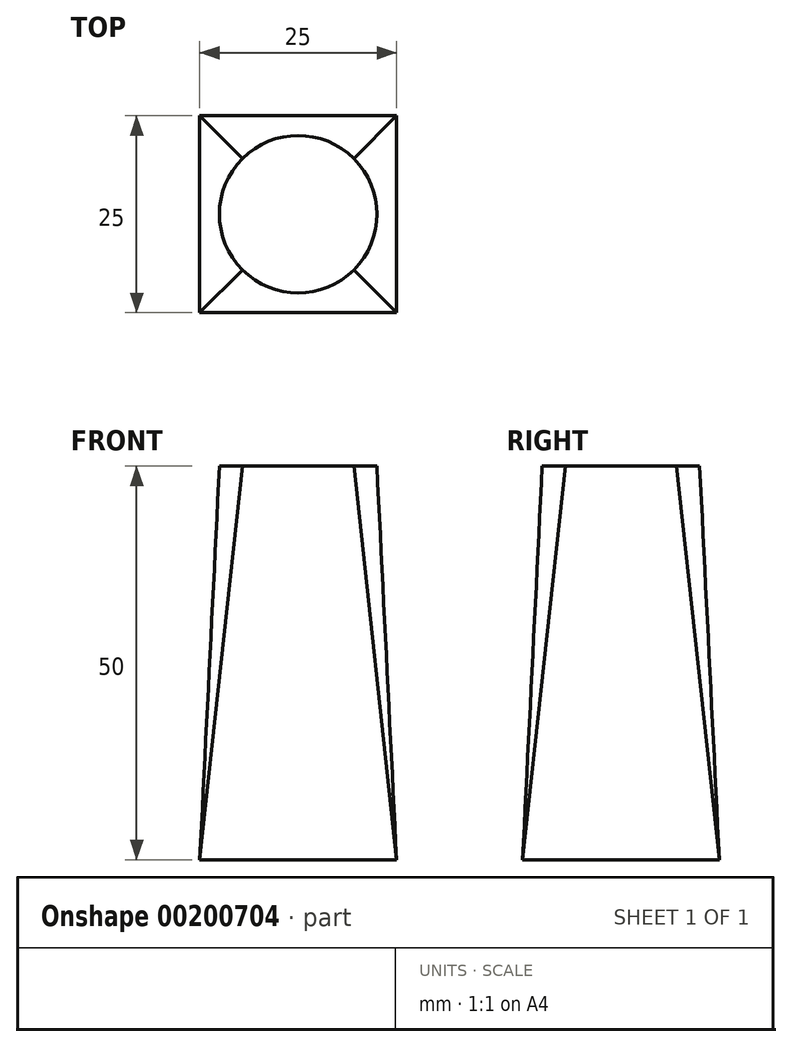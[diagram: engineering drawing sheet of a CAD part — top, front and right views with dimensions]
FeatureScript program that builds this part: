
annotation { "Feature Type Name" : "Feature", "Feature Type Description" : "" }
export const myFeature = defineFeature(function(context is Context, id is Id, definition is map)
    precondition{}
    {
        {
            var Q0;
            Q0=qCreatedBy(makeId("Top.planeOp"),FACE);
            var sketch = newSketch(context, id + "F0", { "sketchPlane" : qUnion([Q0])});
            skLineSegment(sketch, "E0.bottom", {"start": v(-24.37, -23.4) * mm, "end": v(0.63, -23.4) * mm});
            skLineSegment(sketch, "E0.top", {"start": v(-24.37, 1.6) * mm, "end": v(0.63, 1.6) * mm});
            skLineSegment(sketch, "E0.left", {"start": v(-24.37, -23.4) * mm, "end": v(-24.37, 1.6) * mm});
            skLineSegment(sketch, "E0.right", {"start": v(0.63, -23.4) * mm, "end": v(0.63, 1.6) * mm});
            skSolve(sketch);
        }
        {
            var Q0;
            Q0=qCreatedBy(makeId("Top.planeOp"),FACE);
            cPlane(context, id + "F1", {"entities" : qUnion([Q0]), "cplaneType" : CPlaneType.OFFSET, "offset" : 50 * mm, "width" : 150 * mm, "height" : 150 * mm});
        }
        {
            var Q0;
            Q0=qCreatedBy(id+"F1.planeOp",FACE);
            var sketch = newSketch(context, id + "F2", { "sketchPlane" : qUnion([Q0])});
            skCircle(sketch, "E1", {"center": v(-11.87, -10.9) * mm, "radius": 10 * mm});
            skLineSegment(sketch, "E2", {"start": v(-11.87, 1.6) * mm, "end": v(-11.87, -23.4) * mm, "construction": true});
            skSolve(sketch);
        }
        {
            var Q0;
            Q0=makeQuery(id+"F0.imprint","IMPRINT",FACE,{"disambiguationData":[TD([[makeQuery(id+"F0.imprint","IMPRINT",EDGE,{"derivedFrom":sQuery(id+"F0.wireOp",EDGE,"E0.bottom")}),1.0]])]});
            var Q1;
            Q1=makeQuery(id+"F2.imprint","IMPRINT",FACE,{"disambiguationData":[TD([[makeQuery(id+"F2.imprint","IMPRINT",EDGE,{"derivedFrom":sQuery(id+"F2.wireOp",EDGE,"E1")}),1.0]])]});
            loft(context, id + "F3", {"sheetProfilesArray" : [{ "sheetProfileEntities" : qUnion([Q0]) }, { "sheetProfileEntities" : qUnion([Q1]) }]});
        }
    });
